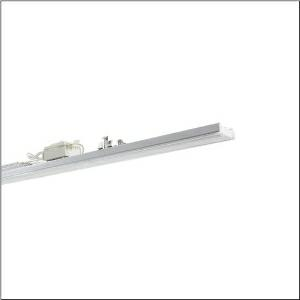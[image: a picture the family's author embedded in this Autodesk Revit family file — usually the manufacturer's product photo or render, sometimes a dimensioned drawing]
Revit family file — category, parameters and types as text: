
# Revit family: licross_r__11_recessed_mo_51tl19dn495g_dc4d
name_source: partatom
category: Lighting Fixtures
units: mm (PartAtom-declared; Revit-internal decimal feet)

## family parameters
Cut with Voids When Loaded = No
Host = Face
Light Source = No
Part Type = Normal
Room Calculation Point = No
Round Connector Dimension = Use Diameter
Shared = No

## types (1)
- --- (1 x LED, 9810 lm, 56.7 W, 4000K)
    Apparent Load = 57 VA
    CIE Flux Codes = 55 90 98 100 100
    Color Rendering = 80
    Color Temperature = 4000K
    Default Elevation = 1800 mm
    Description = Licross® 11 Recessed MO, luminaire insert, of sheet steel, coil coated, white, length: 1.500mm, width: 66mm, height: 67mm, LED rated luminous flux: 9.810lm, light colour: 840, control gear: DALI 2, with plug, 5-pole, with phase selection, mains connection: 220..240V, AC, 50/60Hz, rated input power: 57W, internal wiring halogen-free, primary light control with lens, of plastic, primary optical cover: cover, of PMMA, light emission: direct distribution, primary light characteristic: double asymmetric, protection rating (complete): IP40, insulation class (complete): insulation class I (protective earthing), certification: CE, ENEC, VDE, UKCA, protection symbol: D if used in an environment without relevant dust loads with corresponding accessories, impact resistance: IK06, permissible ambient temperature for indoor applications: -25..+35°C, corresponds to IFS (International Featured Standards) requirements for safety and quality in the food industry, reducing of maximum allowable ambient temperature of 5°C with ceiling mounting, LABS conformity tested according to VDMA 24364:2018-05, packaging unit: 1 piece
    Height = 58 mm
    Lamp = 1 x LED
    Lamp Light Flux = 9810 lm
    Lamp Power = 56.7 W
    Lamp count = 1
    Length = 1500 mm
    Luminous efficacy = 173 lm/W
    Manufacturer = Siteco
    ModVariant = No
    Model = 51TL19DN495G
    Mounting Place = Ceiling
    Mounting Type = Pendant
    Number of Poles = 1
    OnlyDefault = Yes
    Power Factor = 1
    Product Name = Licross® 11 Recessed MO
    Product group = luminaire insert | ceiling pendant
    ProductGroupID = 902
    Protection Class = Protection class I
    Protection Degree = IP 40
    RLX_Detail_Level = 1
    RLX_Emergency_Light_Flux = 0 lm
    RLX_Emergency_Type = 0
    RLX_Emergency_Type_DB = No
    RlxData = <blob elided: 24577 chars, md5=e802a14c>
    Socket = socket
    Standby Power = 0 W
    System Light Flux = 9810 lm
    System Power = 57 W
    Type Comments = factory setting: luminous flux: 100 % | dim-lin: 254 | 378 mA
    Type Image = l_1296930.jpg
    URL = http://relux.com
    VarID = @adj_122239
    Voltage = 0 V
    Weight = 0.00 kg
    Width = 66 mm

## geometry (parser evidence)
native form markers: Blend x4, Sweep x12
no freeform markers — native parametric forms only
